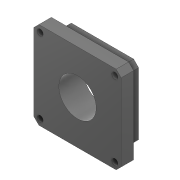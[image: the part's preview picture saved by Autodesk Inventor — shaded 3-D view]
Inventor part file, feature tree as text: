
AUTODESK INVENTOR PART (.ipt)
format: ipt  version: 2020.3 (Build 243373010, 373A)  size: 121,856 bytes
history: native  units: mm
features: extrude x2, sketch x2
ambient origin geometry x8: Origin, YZ Plane, XZ Plane, XY Plane, X Axis, Y Axis, Z Axis, Center Point
bodies: Body1 (feature_tree)
feature tree (4):
  extrude  "Extrusion4"  Depth=5.0mm
  extrude  "Extrusion5"  [1 undecoded]
  sketch  "Sketch5"  dims[d56=5.0mm d57=0.0mm d59=15.0mm]
  sketch  "Sketch6"  dims[d60=5.0mm d61=0.0mm]
note: 1 required parameter value undecoded (feature->parameter linkage not recoverable at this tier; creation-order binding heuristic only, values carry confidence <= 0.55)
